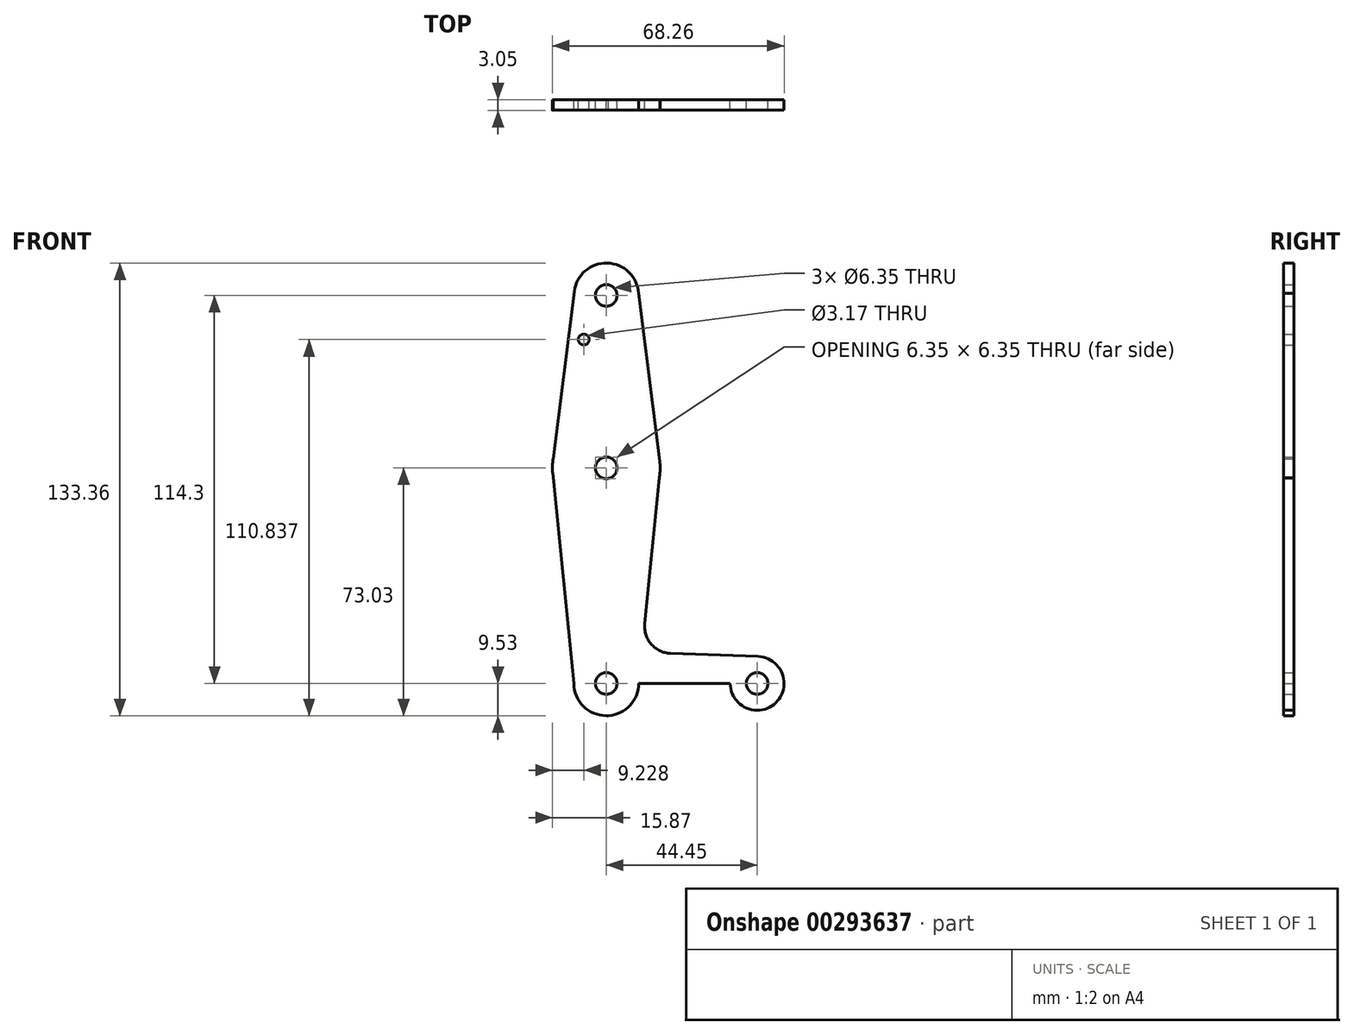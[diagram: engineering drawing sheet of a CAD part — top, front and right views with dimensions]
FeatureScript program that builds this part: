
annotation { "Feature Type Name" : "Feature", "Feature Type Description" : "" }
export const myFeature = defineFeature(function(context is Context, id is Id, definition is map)
    precondition{}
    {
        {
            var Q0;
            Q0=qCreatedBy(makeId("Front.planeOp"),FACE);
            var sketch = newSketch(context, id + "F0", { "sketchPlane" : qUnion([Q0])});
            skCircle(sketch, "E0", {"center": v(0, 0) * mm, "radius": 9.53 * mm});
            skCircle(sketch, "E1", {"center": v(0, 114.3) * mm, "radius": 9.53 * mm});
            skCircle(sketch, "E2", {"center": v(0, 63.5) * mm, "radius": 15.88 * mm});
            skLineSegment(sketch, "E3", {"start": v(0, 0) * mm, "end": v(44.45, 0) * mm});
            skCircle(sketch, "E4", {"center": v(44.45, 0) * mm, "radius": 7.94 * mm});
            skLineSegment(sketch, "E5", {"start": v(0, 63.5) * mm, "end": v(0, 0) * mm});
            skLineSegment(sketch, "E6", {"start": v(0, 63.5) * mm, "end": v(0, 114.3) * mm});
            skLineSegment(sketch, "E7", {"start": v(15.6, 60.53) * mm, "end": v(11.32, 17.58) * mm});
            skLineSegment(sketch, "E8", {"start": v(-15.66, 66.1) * mm, "end": v(-9.45, 115.49) * mm});
            skLineSegment(sketch, "E9", {"start": v(0, -9.53) * mm, "end": v(44.73, -7.93) * mm});
            skLineSegment(sketch, "E10", {"start": v(18.95, 8.85) * mm, "end": v(44.73, 7.93) * mm});
            skLineSegment(sketch, "E11", {"start": v(9.5, 114.9) * mm, "end": v(15.75, 65.5) * mm});
            skCircle(sketch, "E12", {"center": v(0, 114.3) * mm, "radius": 3.18 * mm});
            skCircle(sketch, "E13", {"center": v(-6.64, 101.3) * mm, "radius": 1.59 * mm});
            skCircle(sketch, "E14", {"center": v(0, 63.5) * mm, "radius": 3.18 * mm});
            skCircle(sketch, "E15", {"center": v(0, 0) * mm, "radius": 3.18 * mm});
            skCircle(sketch, "E16", {"center": v(44.45, 0) * mm, "radius": 3.18 * mm});
            skArc(sketch, "E17.filletArc", {"start": v(11.32, 17.58) * mm, "mid": v(13.25, 11.57) * mm, "end": v(18.95, 8.85) * mm});
            skLineSegment(sketch, "E18", {"start": v(-9.53, 0) * mm, "end": v(-15.8, 61.9) * mm});
            skSolve(sketch);
        }
        {
            var Q0;
            {var subQ5=sQuery(id+"F0.wireOp",EDGE,"E8");Q0=makeQuery(id+"F0.imprint","IMPRINT",FACE,{"disambiguationData":[TD([[makeQuery(id+"F0.imprint","IMPRINT",EDGE,{"derivedFrom":subQ5}),-1.0]])]});}
            var Q1;
            {var subQ0=sQuery(id+"F0.wireOp",EDGE,"E11");Q1=makeQuery(id+"F0.imprint","IMPRINT",FACE,{"disambiguationData":[TD([[makeQuery(id+"F0.imprint","IMPRINT",EDGE,{"derivedFrom":subQ0}),-1.0]])]});}
            var Q2;
            Q2=makeQuery(id+"F0.imprint","IMPRINT",FACE,{"disambiguationData":[TD([[makeQuery(id+"F0.imprint","IMPRINT",EDGE,{"derivedFrom":sQuery(id+"F0.wireOp",EDGE,"E12")}),-1.0]])]});
            var Q3;
            {var subQ1=sQuery(id+"F0.wireOp",EDGE,"E2");var subQ5=makeQuery(id+"F0.imprint","INTERSECT",VERTEX,{"derivedFrom":[subQ1,sQuery(id+"F0.wireOp",EDGE,"E8")]});Q3=makeQuery(id+"F0.imprint","IMPRINT",FACE,{"disambiguationData":[TD([[makeQuery(id+"F0.imprint","IMPRINT",EDGE,{"disambiguationData":[TD([[subQ5,1.0]])],"derivedFrom":subQ1}),1.0]])]});}
            var Q4;
            {var subQ1=sQuery(id+"F0.wireOp",EDGE,"E2");var subQ6=makeQuery(id+"F0.imprint","INTERSECT",VERTEX,{"derivedFrom":[subQ1,sQuery(id+"F0.wireOp",EDGE,"E11")]});Q4=makeQuery(id+"F0.imprint","IMPRINT",FACE,{"disambiguationData":[TD([[makeQuery(id+"F0.imprint","IMPRINT",EDGE,{"disambiguationData":[TD([[subQ6,-1.0]])],"derivedFrom":subQ1}),1.0]])]});}
            var Q5;
            {var subQ6=sQuery(id+"F0.wireOp",EDGE,"E7");Q5=makeQuery(id+"F0.imprint","IMPRINT",FACE,{"disambiguationData":[TD([[makeQuery(id+"F0.imprint","IMPRINT",EDGE,{"derivedFrom":subQ6}),-1.0]])]});}
            var Q6;
            {var subQ0=sQuery(id+"F0.wireOp",EDGE,"E18");Q6=makeQuery(id+"F0.imprint","IMPRINT",FACE,{"disambiguationData":[TD([[makeQuery(id+"F0.imprint","IMPRINT",EDGE,{"derivedFrom":subQ0}),-1.0]])]});}
            var Q7;
            {var subQ1=sQuery(id+"F0.wireOp",EDGE,"E0");var subQ8=makeQuery(id+"F0.imprint","INTERSECT",VERTEX,{"derivedFrom":[subQ1,sQuery(id+"F0.wireOp",EDGE,"E18")]});Q7=makeQuery(id+"F0.imprint","IMPRINT",FACE,{"disambiguationData":[TD([[makeQuery(id+"F0.imprint","IMPRINT",EDGE,{"disambiguationData":[TD([[subQ8,1.0]])],"derivedFrom":subQ1}),1.0]])]});}
            var Q8;
            {var subQ0=sQuery(id+"F0.wireOp",EDGE,"E5");var subQ1=sQuery(id+"F0.wireOp",EDGE,"E0");var subQ2=makeQuery(id+"F0.imprint","INTERSECT",VERTEX,{"derivedFrom":[subQ1,subQ0]});Q8=makeQuery(id+"F0.imprint","IMPRINT",FACE,{"disambiguationData":[TD([[makeQuery(id+"F0.imprint","IMPRINT",EDGE,{"disambiguationData":[TD([[subQ2,1.0]])],"derivedFrom":subQ1}),1.0]])]});}
            var Q9;
            {var subQ0=sQuery(id+"F0.wireOp",EDGE,"E9");var subQ1=sQuery(id+"F0.wireOp",EDGE,"E0");var subQ2=makeQuery(id+"F0.imprint","INTERSECT",VERTEX,{"disambiguationData":[OD(1.0)],"derivedFrom":[subQ1,subQ0]});Q9=makeQuery(id+"F0.imprint","IMPRINT",FACE,{"disambiguationData":[TD([[makeQuery(id+"F0.imprint","IMPRINT",EDGE,{"disambiguationData":[TD([[subQ2,-1.0]])],"derivedFrom":subQ1}),-1.0]])]});}
            var Q10;
            Q10=makeQuery(id+"F0.imprint","IMPRINT",FACE,{"disambiguationData":[TD([[makeQuery(id+"F0.imprint","IMPRINT",EDGE,{"derivedFrom":sQuery(id+"F0.wireOp",EDGE,"E16")}),-1.0]])]});
            extrude(context, id + "F1", {"entities" : qUnion([Q0, Q1, Q2, Q3, Q4, Q5, Q6, Q7, Q8, Q9, Q10]), "depth" : 3.05 * mm});
        }
    });
